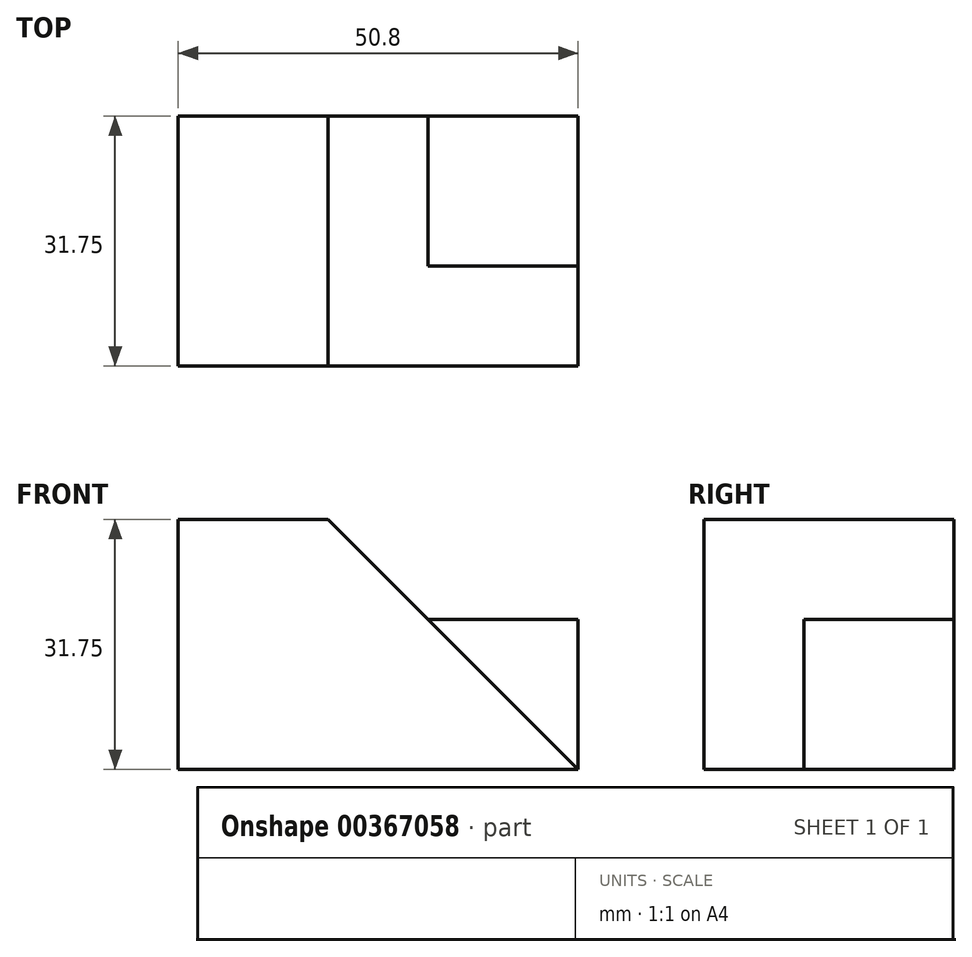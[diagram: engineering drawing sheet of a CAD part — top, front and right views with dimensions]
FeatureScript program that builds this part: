
annotation { "Feature Type Name" : "Feature", "Feature Type Description" : "" }
export const myFeature = defineFeature(function(context is Context, id is Id, definition is map)
    precondition{}
    {
        {
            var Q0;
            Q0=qCreatedBy(makeId("Front.planeOp"),FACE);
            var sketch = newSketch(context, id + "F0", { "sketchPlane" : qUnion([Q0])});
            skLineSegment(sketch, "E0", {"start": v(-50.8, 0) * mm, "end": v(0, 0) * mm});
            skLineSegment(sketch, "E1", {"start": v(0, 0) * mm, "end": v(0, 31.75) * mm});
            skLineSegment(sketch, "E2", {"start": v(0, 31.75) * mm, "end": v(-50.8, 31.75) * mm});
            skLineSegment(sketch, "E3", {"start": v(-50.8, 31.75) * mm, "end": v(-50.8, 0) * mm});
            skSolve(sketch);
        }
        {
            var Q0;
            Q0=makeQuery(id+"F0.imprint","IMPRINT",FACE,{"disambiguationData":[TD([[makeQuery(id+"F0.imprint","IMPRINT",EDGE,{"derivedFrom":sQuery(id+"F0.wireOp",EDGE,"E0")}),1.0]])]});
            extrude(context, id + "F1", {"entities" : qUnion([Q0]), "depth" : 31.75 * mm});
        }
        {
            var Q0;
            Q0=makeQuery(id+"F1.opExtrude","CAP_FACE",FACE,{"disambiguationData":[OSD([sQuery(id+"F0.wireOp",EDGE,"E0"),sQuery(id+"F0.wireOp",EDGE,"E1"),sQuery(id+"F0.wireOp",EDGE,"E2"),sQuery(id+"F0.wireOp",EDGE,"E3")])],"isStart":false});
            var sketch = newSketch(context, id + "F2", { "sketchPlane" : qUnion([Q0])});
            skLineSegment(sketch, "E4", {"start": v(-31.75, 31.75) * mm, "end": v(0, 0) * mm});
            skLineSegment(sketch, "E5", {"start": v(-31.75, 31.75) * mm, "end": v(0, 31.75) * mm});
            skLineSegment(sketch, "E6", {"start": v(0, 31.75) * mm, "end": v(0, 0) * mm});
            skSolve(sketch);
        }
        {
            var Q0;
            Q0=makeQuery(id+"F2.imprint","IMPRINT",FACE,{"disambiguationData":[TD([[makeQuery(id+"F2.imprint","IMPRINT",EDGE,{"derivedFrom":sQuery(id+"F2.wireOp",EDGE,"E4")}),1.0]])]});
            extrude(context, id + "F3", {"entities" : qUnion([Q0]), "operationType" : NewBodyOperationType.REMOVE, "oppositeDirection" : true, "depth" : 31.75 * mm});
        }
        {
            var Q0;
            Q0=qCreatedBy(makeId("Front.planeOp"),FACE);
            var sketch = newSketch(context, id + "F4", { "sketchPlane" : qUnion([Q0])});
            skLineSegment(sketch, "E7", {"start": v(-19.05, 19.05) * mm, "end": v(-19.05, 19.87) * mm});
            skLineSegment(sketch, "E8", {"start": v(-19.05, 19.05) * mm, "end": v(0, 19.05) * mm});
            skLineSegment(sketch, "E9", {"start": v(0, 19.05) * mm, "end": v(0, 0) * mm});
            skLineSegment(sketch, "E10", {"start": v(0, 0) * mm, "end": v(-19.05, 19.05) * mm});
            skSolve(sketch);
        }
        {
            var Q0;
            Q0=makeQuery(id+"F4.imprint","IMPRINT",FACE,{"disambiguationData":[TD([[makeQuery(id+"F4.imprint","IMPRINT",EDGE,{"derivedFrom":sQuery(id+"F4.wireOp",EDGE,"E8")}),-1.0]])]});
            extrude(context, id + "F5", {"entities" : qUnion([Q0]), "operationType" : NewBodyOperationType.ADD, "depth" : 19.05 * mm});
        }
    });
